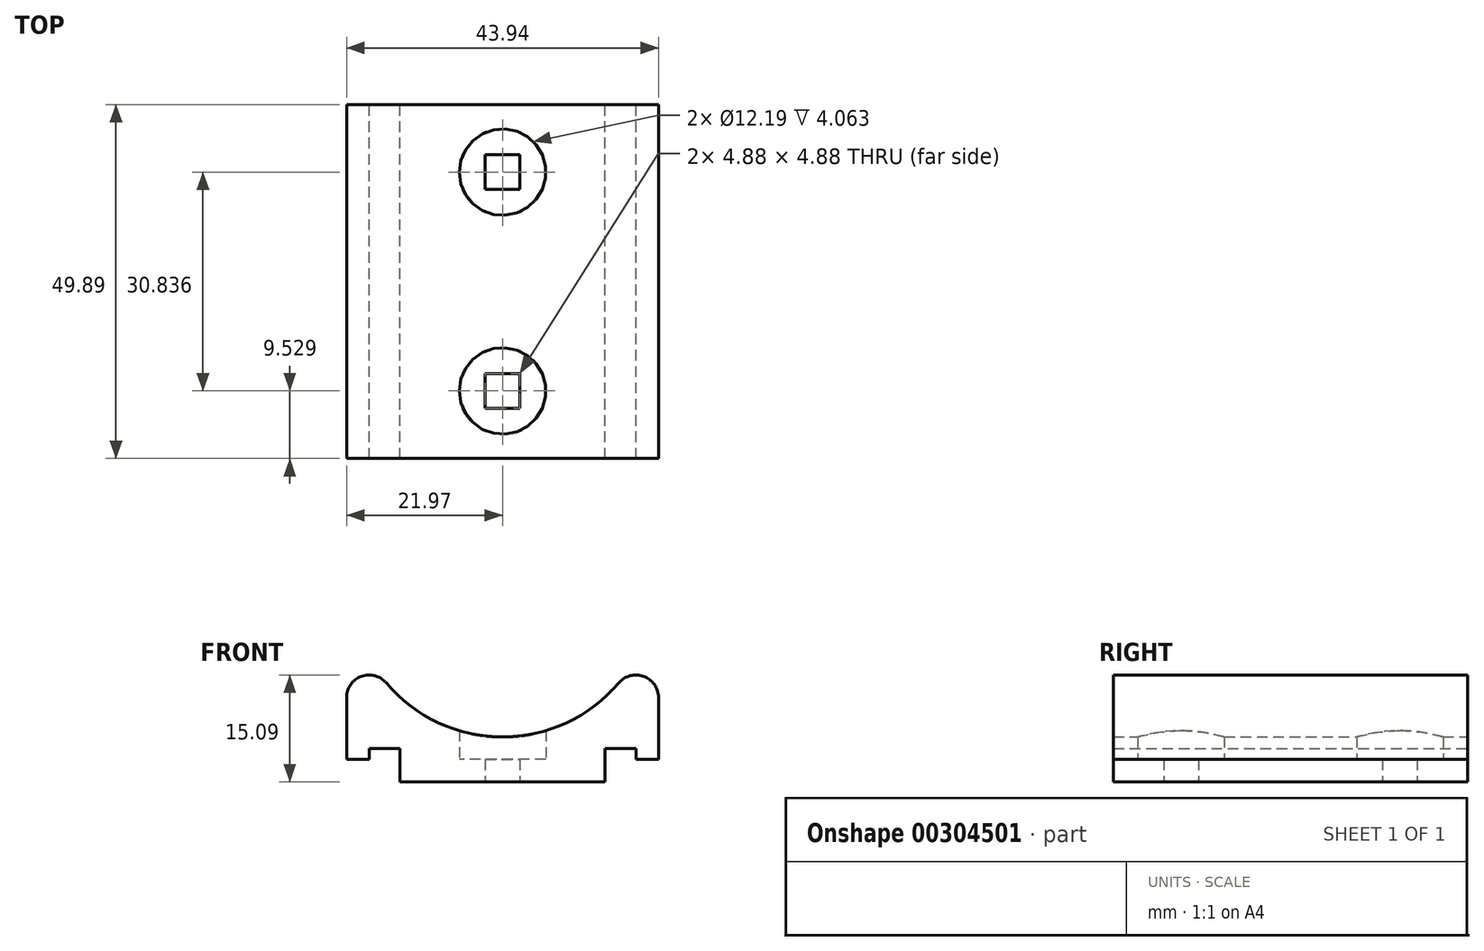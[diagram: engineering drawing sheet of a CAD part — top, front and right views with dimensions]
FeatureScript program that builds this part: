
annotation { "Feature Type Name" : "Feature", "Feature Type Description" : "" }
export const myFeature = defineFeature(function(context is Context, id is Id, definition is map)
    precondition{}
    {
        {
            var Q0;
            Q0=qCreatedBy(makeId("Front.planeOp"),FACE);
            var sketch = newSketch(context, id + "F0", { "sketchPlane" : qUnion([Q0])});
            skLineSegment(sketch, "E0", {"start": v(-21.97, -3.17) * mm, "end": v(-18.8, -3.17) * mm});
            skLineSegment(sketch, "E1", {"start": v(-18.8, -3.17) * mm, "end": v(-18.8, -1.65) * mm});
            skLineSegment(sketch, "E2", {"start": v(-18.8, -1.65) * mm, "end": v(-14.43, -1.65) * mm});
            skLineSegment(sketch, "E3", {"start": v(-14.43, -1.65) * mm, "end": v(-14.43, -6.35) * mm});
            skLineSegment(sketch, "E4", {"start": v(-14.43, -6.35) * mm, "end": v(0, -6.35) * mm});
            skLineSegment(sketch, "E5", {"start": v(0, -6.35) * mm, "end": v(0, 0) * mm, "construction": true});
            skLineSegment(sketch, "E6", {"start": v(-21.97, -3.17) * mm, "end": v(-21.97, 5.57) * mm});
            skArc(sketch, "E7", {"start": v(-21.97, 5.57) * mm, "mid": v(-19.89, 8.55) * mm, "end": v(-16.38, 7.61) * mm});
            skArc(sketch, "E8", {"start": v(-16.38, 7.61) * mm, "mid": v(-9.03, 2) * mm, "end": v(0, 0) * mm});
            skLineSegment(sketch, "E9", {"start": v(-35.08, 8.74) * mm, "end": v(-8.37, 8.74) * mm, "construction": true});
            skArc(sketch, "E10.MirrorCS", {"start": v(21.97, 5.57) * mm, "mid": v(19.89, 8.55) * mm, "end": v(16.38, 7.61) * mm});
            skArc(sketch, "E11.MirrorCS", {"start": v(16.38, 7.61) * mm, "mid": v(9.03, 2) * mm, "end": v(0, 0) * mm});
            skLineSegment(sketch, "E12.MirrorCS", {"start": v(21.97, -3.17) * mm, "end": v(21.97, 5.57) * mm});
            skLineSegment(sketch, "E13.MirrorCS", {"start": v(21.97, -3.17) * mm, "end": v(18.8, -3.17) * mm});
            skLineSegment(sketch, "E14.MirrorCS", {"start": v(18.8, -3.17) * mm, "end": v(18.8, -1.65) * mm});
            skLineSegment(sketch, "E15.MirrorCS", {"start": v(18.8, -1.65) * mm, "end": v(14.43, -1.65) * mm});
            skLineSegment(sketch, "E16.MirrorCS", {"start": v(14.43, -1.65) * mm, "end": v(14.43, -6.35) * mm});
            skLineSegment(sketch, "E17.MirrorCS", {"start": v(14.43, -6.35) * mm, "end": v(0, -6.35) * mm});
            skSolve(sketch);
        }
        {
            var Q0;
            Q0=makeQuery(id+"F0.imprint","IMPRINT",FACE,{"disambiguationData":[TD([[makeQuery(id+"F0.imprint","IMPRINT",EDGE,{"derivedFrom":sQuery(id+"F0.wireOp",EDGE,"E0")}),1.0]])]});
            extrude(context, id + "F1", {"entities" : qUnion([Q0]), "depth" : 49.9 * mm});
        }
        {
            var Q0;
            Q0=qCreatedBy(makeId("Top.planeOp"),FACE);
            var sketch = newSketch(context, id + "F2", { "sketchPlane" : qUnion([Q0])});
            skCircle(sketch, "E18", {"center": v(0, -9.53) * mm, "radius": 6.1 * mm});
            skCircle(sketch, "E19", {"center": v(0, -40.36) * mm, "radius": 6.1 * mm});
            skCircle(sketch, "E20.cCircle", {"center": v(0, -9.53) * mm, "radius": 2.44 * mm, "construction": true});
            skLineSegment(sketch, "E20.0", {"start": v(2.44, -7.09) * mm, "end": v(2.44, -11.96) * mm});
            skLineSegment(sketch, "E20.1", {"start": v(2.44, -11.96) * mm, "end": v(-2.44, -11.96) * mm});
            skLineSegment(sketch, "E20.2", {"start": v(-2.44, -11.96) * mm, "end": v(-2.44, -7.09) * mm});
            skLineSegment(sketch, "E20.3", {"start": v(-2.44, -7.09) * mm, "end": v(2.44, -7.09) * mm});
            skPoint(sketch, "E20.0.midPoint", {"position": v(2.44, -9.53) * mm});
            skCircle(sketch, "E21.cCircle", {"center": v(0, -40.36) * mm, "radius": 2.44 * mm, "construction": true});
            skLineSegment(sketch, "E21.0", {"start": v(2.44, -37.92) * mm, "end": v(2.44, -42.8) * mm});
            skLineSegment(sketch, "E21.1", {"start": v(2.44, -42.8) * mm, "end": v(-2.44, -42.8) * mm});
            skLineSegment(sketch, "E21.2", {"start": v(-2.44, -42.8) * mm, "end": v(-2.44, -37.92) * mm});
            skLineSegment(sketch, "E21.3", {"start": v(-2.44, -37.92) * mm, "end": v(2.44, -37.92) * mm});
            skPoint(sketch, "E21.0.midPoint", {"position": v(2.44, -40.36) * mm});
            skSolve(sketch);
        }
        {
            var Q0;
            Q0=makeQuery(id+"F2.imprint","IMPRINT",FACE,{"disambiguationData":[TD([[makeQuery(id+"F2.imprint","IMPRINT",EDGE,{"derivedFrom":sQuery(id+"F2.wireOp",EDGE,"E20.0")}),-1.0]])]});
            var Q1;
            Q1=makeQuery(id+"F2.imprint","IMPRINT",FACE,{"disambiguationData":[TD([[makeQuery(id+"F2.imprint","IMPRINT",EDGE,{"derivedFrom":sQuery(id+"F2.wireOp",EDGE,"E21.0")}),-1.0]])]});
            extrude(context, id + "F3", {"entities" : qUnion([Q0, Q1]), "operationType" : NewBodyOperationType.REMOVE, "depth" : 25.4 * mm, "hasSecondDirection" : true, "secondDirectionOppositeDirection" : true, "secondDirectionDepth" : 25.4 * mm});
        }
        {
            var Q0;
            Q0=makeQuery(id+"F2.imprint","IMPRINT",FACE,{"disambiguationData":[TD([[makeQuery(id+"F2.imprint","IMPRINT",EDGE,{"derivedFrom":sQuery(id+"F2.wireOp",EDGE,"E19")}),1.0]])]});
            var Q1;
            Q1=makeQuery(id+"F2.imprint","IMPRINT",FACE,{"disambiguationData":[TD([[makeQuery(id+"F2.imprint","IMPRINT",EDGE,{"derivedFrom":sQuery(id+"F2.wireOp",EDGE,"E18")}),1.0]])]});
            var Q2;
            Q2=makeQuery(id+"F2.imprint","IMPRINT",FACE,{"disambiguationData":[TD([[makeQuery(id+"F2.imprint","IMPRINT",EDGE,{"derivedFrom":sQuery(id+"F2.wireOp",EDGE,"E21.0")}),-1.0]])]});
            var Q3;
            Q3=makeQuery(id+"F2.imprint","IMPRINT",FACE,{"disambiguationData":[TD([[makeQuery(id+"F2.imprint","IMPRINT",EDGE,{"derivedFrom":sQuery(id+"F2.wireOp",EDGE,"E20.0")}),-1.0]])]});
            extrude(context, id + "F4", {"entities" : qUnion([Q0, Q1, Q2, Q3]), "operationType" : NewBodyOperationType.REMOVE, "endBound" : BoundingType.THROUGH_ALL, "depth" : 25.4 * mm, "hasSecondDirection" : true, "secondDirectionOppositeDirection" : true, "secondDirectionDepth" : 3.17 * mm});
        }
    });
